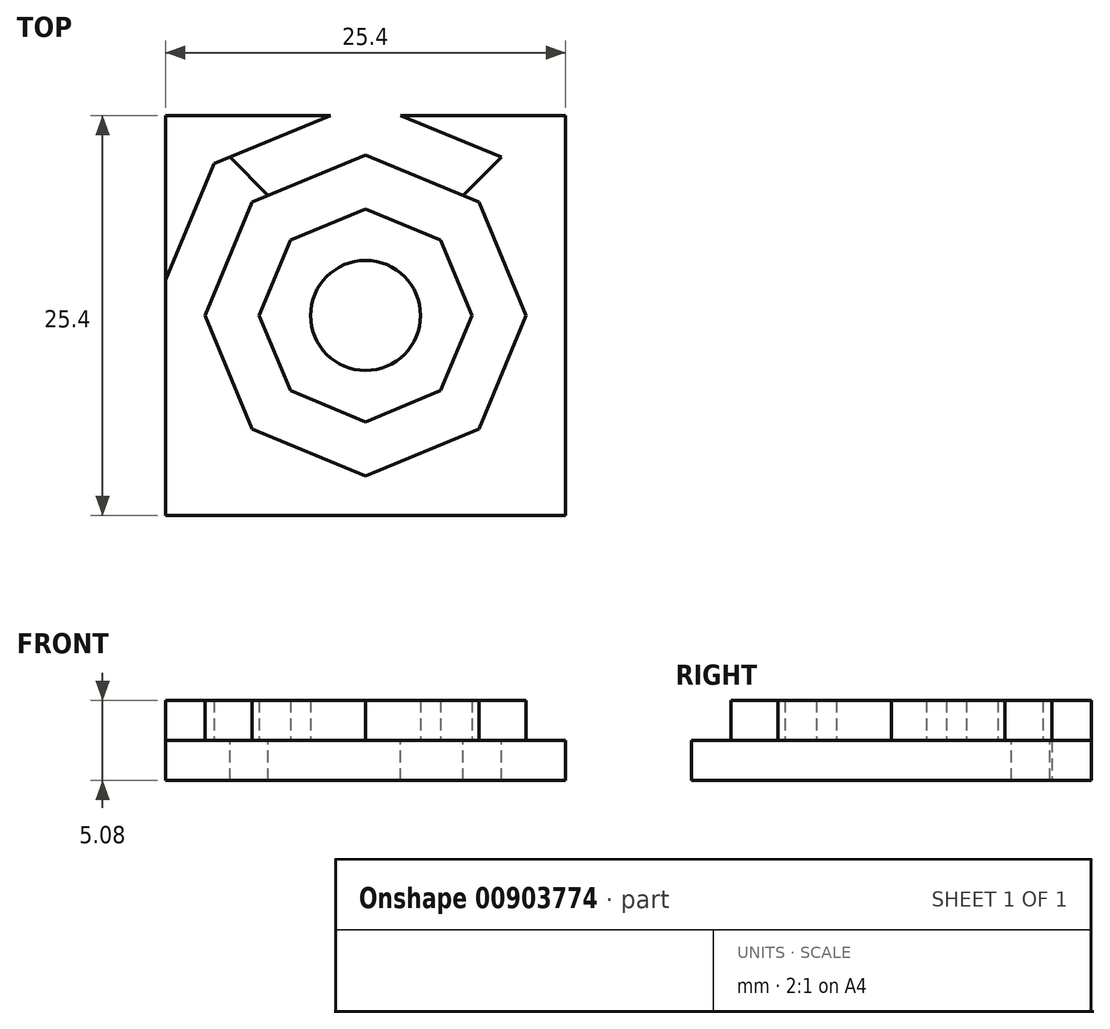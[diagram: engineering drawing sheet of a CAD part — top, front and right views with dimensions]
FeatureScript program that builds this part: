
annotation { "Feature Type Name" : "Feature", "Feature Type Description" : "" }
export const myFeature = defineFeature(function(context is Context, id is Id, definition is map)
    precondition{}
    {
        {
            var Q0;
            Q0=qCreatedBy(makeId("Top.planeOp"),FACE);
            var sketch = newSketch(context, id + "F0", { "sketchPlane" : qUnion([Q0])});
            skLineSegment(sketch, "E0.bottom", {"start": v(-12.7, 12.7) * mm, "end": v(12.7, 12.7) * mm});
            skLineSegment(sketch, "E0.top", {"start": v(-12.7, -12.7) * mm, "end": v(12.7, -12.7) * mm});
            skLineSegment(sketch, "E0.left", {"start": v(-12.7, 12.7) * mm, "end": v(-12.7, -12.7) * mm});
            skLineSegment(sketch, "E0.right", {"start": v(12.7, 12.7) * mm, "end": v(12.7, -12.7) * mm});
            skPoint(sketch, "E0.middle", {"position": v(0, 0) * mm});
            skSolve(sketch);
        }
        {
            var Q0;
            Q0=qSketchRegion(id+"F0",true);
            extrude(context, id + "F1", {"entities" : qUnion([Q0]), "endBound" : BoundingType.SYMMETRIC, "depth" : 2.54 * mm, "offsetDistance" : 25.4 * mm});
        }
        {
            var Q0;
            Q0=makeQuery(id+"F1.opExtrude","CAP_FACE",FACE,{"disambiguationData":[OSD([sQuery(id+"F0.wireOp",EDGE,"E0.bottom"),sQuery(id+"F0.wireOp",EDGE,"E0.top"),sQuery(id+"F0.wireOp",EDGE,"E0.left"),sQuery(id+"F0.wireOp",EDGE,"E0.right")])],"isStart":false});
            var sketch = newSketch(context, id + "F2", { "sketchPlane" : qUnion([Q0])});
            skLineSegment(sketch, "E1", {"start": v(-12.7, 12.7) * mm, "end": v(-12.7, 2.24) * mm});
            skLineSegment(sketch, "E2", {"start": v(-12.7, 12.7) * mm, "end": v(12.7, -12.7) * mm, "construction": true});
            skLineSegment(sketch, "E3", {"start": v(12.7, -12.7) * mm, "end": v(12.7, 12.7) * mm, "construction": true});
            skLineSegment(sketch, "E4", {"start": v(12.7, 12.7) * mm, "end": v(-12.7, -12.7) * mm, "construction": true});
            skLineSegment(sketch, "E5", {"start": v(-12.7, 2.24) * mm, "end": v(-9.63, 9.63) * mm});
            skLineSegment(sketch, "E6", {"start": v(-9.63, 9.63) * mm, "end": v(-2.24, 12.7) * mm});
            skLineSegment(sketch, "E7", {"start": v(-2.24, 12.7) * mm, "end": v(-12.7, 12.7) * mm});
            skLineSegment(sketch, "E8", {"start": v(-7.2, 7.2) * mm, "end": v(0, 10.19) * mm});
            skLineSegment(sketch, "E9", {"start": v(-7.2, 7.2) * mm, "end": v(-10.19, 0) * mm});
            skLineSegment(sketch, "E10", {"start": v(-10.19, 0) * mm, "end": v(-7.2, -7.2) * mm});
            skLineSegment(sketch, "E11", {"start": v(-7.2, -7.2) * mm, "end": v(0, -10.19) * mm});
            skLineSegment(sketch, "E12", {"start": v(0, -10.19) * mm, "end": v(7.2, -7.2) * mm});
            skLineSegment(sketch, "E13", {"start": v(7.2, -7.2) * mm, "end": v(10.19, 0) * mm});
            skLineSegment(sketch, "E14", {"start": v(10.19, 0) * mm, "end": v(7.2, 7.2) * mm});
            skLineSegment(sketch, "E15", {"start": v(7.2, 7.2) * mm, "end": v(0, 10.19) * mm});
            skLineSegment(sketch, "E16", {"start": v(0, 6.75) * mm, "end": v(-4.77, 4.77) * mm});
            skLineSegment(sketch, "E17", {"start": v(-4.77, 4.77) * mm, "end": v(-6.75, 0) * mm});
            skLineSegment(sketch, "E18", {"start": v(-6.75, 0) * mm, "end": v(-4.77, -4.77) * mm});
            skLineSegment(sketch, "E19", {"start": v(-4.77, -4.77) * mm, "end": v(0, -6.75) * mm});
            skLineSegment(sketch, "E20", {"start": v(0, -6.75) * mm, "end": v(4.77, -4.77) * mm});
            skLineSegment(sketch, "E21", {"start": v(4.77, -4.77) * mm, "end": v(6.75, 0) * mm});
            skLineSegment(sketch, "E22", {"start": v(6.75, 0) * mm, "end": v(4.77, 4.77) * mm});
            skLineSegment(sketch, "E23", {"start": v(4.77, 4.77) * mm, "end": v(0, 6.75) * mm});
            skCircle(sketch, "E24", {"center": v(0, 0) * mm, "radius": 3.5 * mm});
            skSolve(sketch);
        }
        {
            var Q0;
            Q0=makeQuery(id+"F2.imprint","IMPRINT",FACE,{"disambiguationData":[TD([[makeQuery(id+"F2.imprint","IMPRINT",EDGE,{"derivedFrom":sQuery(id+"F2.wireOp",EDGE,"E8")}),-1.0]])]});
            extrude(context, id + "F3", {"entities" : qUnion([Q0]), "operationType" : NewBodyOperationType.ADD, "depth" : 2.54 * mm, "offsetDistance" : 25.4 * mm});
        }
        {
            var Q0;
            Q0=makeQuery(id+"F2.imprint","IMPRINT",FACE,{"disambiguationData":[TD([[makeQuery(id+"F2.imprint","IMPRINT",EDGE,{"derivedFrom":sQuery(id+"F2.wireOp",EDGE,"E24")}),1.0]])]});
            var Q1;
            Q1=makeQuery(id+"F3.opExtrude","CAP_FACE",FACE,{"disambiguationData":[OSD([sQuery(id+"F2.wireOp",EDGE,"E8"),sQuery(id+"F2.wireOp",EDGE,"E9"),sQuery(id+"F2.wireOp",EDGE,"E10"),sQuery(id+"F2.wireOp",EDGE,"E11"),sQuery(id+"F2.wireOp",EDGE,"E12"),sQuery(id+"F2.wireOp",EDGE,"E13"),sQuery(id+"F2.wireOp",EDGE,"E14"),sQuery(id+"F2.wireOp",EDGE,"E15"),sQuery(id+"F2.wireOp",EDGE,"E16"),sQuery(id+"F2.wireOp",EDGE,"E17"),sQuery(id+"F2.wireOp",EDGE,"E18"),sQuery(id+"F2.wireOp",EDGE,"E19"),sQuery(id+"F2.wireOp",EDGE,"E20"),sQuery(id+"F2.wireOp",EDGE,"E21"),sQuery(id+"F2.wireOp",EDGE,"E22"),sQuery(id+"F2.wireOp",EDGE,"E23")])],"isStart":false});
            extrude(context, id + "F4", {"entities" : qUnion([Q0]), "operationType" : NewBodyOperationType.ADD, "endBound" : BoundingType.UP_TO_SURFACE, "depth" : 25.4 * mm, "endBoundEntityFace" : qUnion([Q1]), "offsetDistance" : 25.4 * mm});
        }
        {
            var Q0;
            Q0=makeQuery(id+"F2.imprint","IMPRINT",FACE,{"disambiguationData":[TD([[makeQuery(id+"F2.imprint","IMPRINT",EDGE,{"derivedFrom":sQuery(id+"F2.wireOp",EDGE,"E1")}),1.0]])]});
            var Q1;
            Q1=makeQuery(id+"F3.opExtrude","CAP_FACE",FACE,{"disambiguationData":[OSD([sQuery(id+"F2.wireOp",EDGE,"E8"),sQuery(id+"F2.wireOp",EDGE,"E9"),sQuery(id+"F2.wireOp",EDGE,"E10"),sQuery(id+"F2.wireOp",EDGE,"E11"),sQuery(id+"F2.wireOp",EDGE,"E12"),sQuery(id+"F2.wireOp",EDGE,"E13"),sQuery(id+"F2.wireOp",EDGE,"E14"),sQuery(id+"F2.wireOp",EDGE,"E15"),sQuery(id+"F2.wireOp",EDGE,"E16"),sQuery(id+"F2.wireOp",EDGE,"E17"),sQuery(id+"F2.wireOp",EDGE,"E18"),sQuery(id+"F2.wireOp",EDGE,"E19"),sQuery(id+"F2.wireOp",EDGE,"E20"),sQuery(id+"F2.wireOp",EDGE,"E21"),sQuery(id+"F2.wireOp",EDGE,"E22"),sQuery(id+"F2.wireOp",EDGE,"E23")])],"isStart":false});
            extrude(context, id + "F5", {"entities" : qUnion([Q0]), "operationType" : NewBodyOperationType.ADD, "endBound" : BoundingType.UP_TO_SURFACE, "depth" : 25.4 * mm, "endBoundEntityFace" : qUnion([Q1]), "offsetDistance" : 25.4 * mm});
        }
        {
            var Q0;
            {var subQ0=sQuery(id+"F0.wireOp",EDGE,"E0.left");var subQ1=sQuery(id+"F0.wireOp",EDGE,"E0.bottom");var subQ2=sQuery(id+"F0.wireOp",EDGE,"E0.right");var subQ3=sQuery(id+"F0.wireOp",EDGE,"E0.top");Q0=makeQuery(id+"F3.boolean.opBoolean","SPLIT",FACE,{"disambiguationData":[TD([makeQuery(id+"F1.opExtrude","SWEPT_FACE",FACE,{"disambiguationData":[OSD([subQ1])]})])],"derivedFrom":makeQuery(id+"F1.opExtrude","CAP_FACE",FACE,{"disambiguationData":[OSD([subQ1,subQ3,subQ0,subQ2])],"isStart":false})});}
            var sketch = newSketch(context, id + "F6", { "sketchPlane" : qUnion([Q0])});
            skLineSegment(sketch, "E25", {"start": v(-9.63, 9.63) * mm, "end": v(9.63, -9.63) * mm, "construction": true});
            skLineSegment(sketch, "E26", {"start": v(9.63, 9.63) * mm, "end": v(-9.63, -9.63) * mm, "construction": true});
            skLineSegment(sketch, "E27", {"start": v(-6.19, 7.63) * mm, "end": v(-8.62, 10.06) * mm});
            skLineSegment(sketch, "E28.2", {"start": v(-9.63, 9.63) * mm, "end": v(-2.24, 12.7) * mm});
            skLineSegment(sketch, "E29.0", {"start": v(-7.2, 7.2) * mm, "end": v(0, 10.19) * mm});
            skLineSegment(sketch, "E30.0", {"start": v(-2.24, 12.7) * mm, "end": v(2.24, 12.7) * mm});
            skLineSegment(sketch, "E31.0", {"start": v(2.24, 12.7) * mm, "end": v(9.63, 9.63) * mm});
            skLineSegment(sketch, "E32.0", {"start": v(7.2, 7.2) * mm, "end": v(0, 10.19) * mm});
            skLineSegment(sketch, "E33", {"start": v(8.62, 10.06) * mm, "end": v(6.19, 7.63) * mm});
            skSolve(sketch);
        }
        {
            var Q0;
            {var subQ3=sQuery(id+"F6.wireOp",EDGE,"E27");Q0=makeQuery(id+"F6.imprint","IMPRINT",FACE,{"disambiguationData":[TD([[makeQuery(id+"F6.imprint","IMPRINT",EDGE,{"derivedFrom":subQ3}),-1.0]])]});}
            extrude(context, id + "F7", {"entities" : qUnion([Q0]), "operationType" : NewBodyOperationType.REMOVE, "endBound" : BoundingType.THROUGH_ALL, "oppositeDirection" : true, "depth" : 25.4 * mm, "offsetDistance" : 25.4 * mm});
        }
    });
